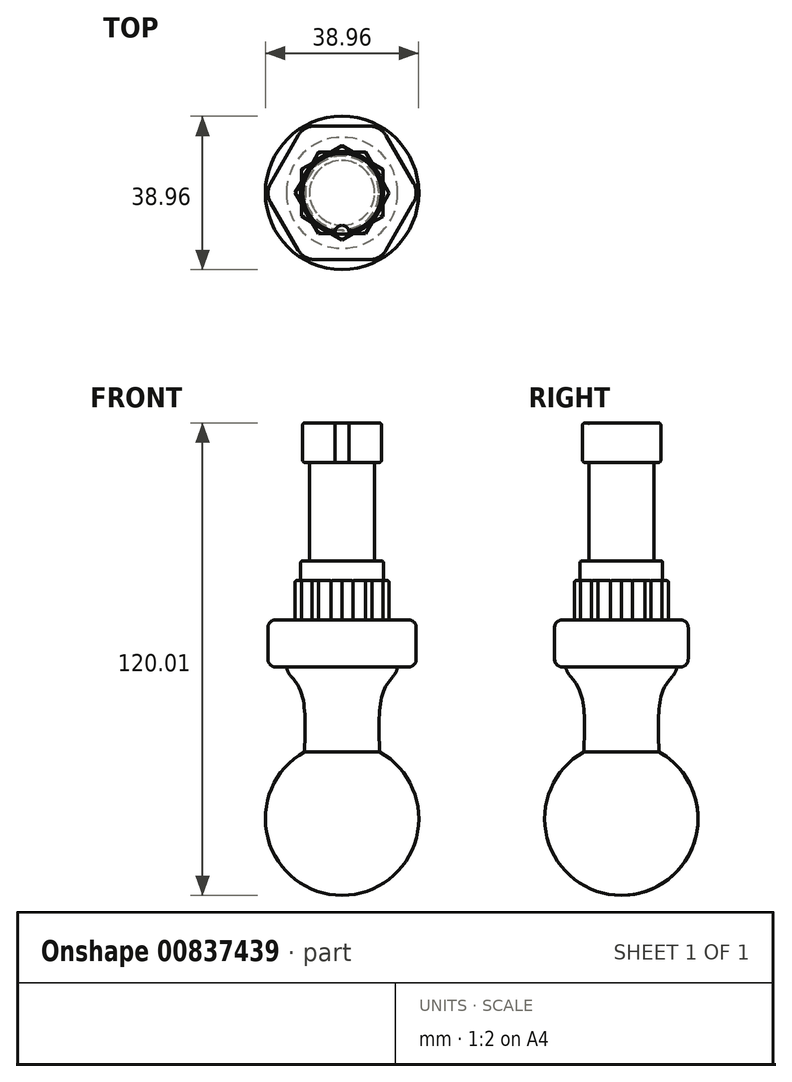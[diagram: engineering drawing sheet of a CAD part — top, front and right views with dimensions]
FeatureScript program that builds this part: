
annotation { "Feature Type Name" : "Feature", "Feature Type Description" : "" }
export const myFeature = defineFeature(function(context is Context, id is Id, definition is map)
    precondition{}
    {
        {
            var Q0;
            Q0=qCreatedBy(makeId("Top.planeOp"),FACE);
            var sketch = newSketch(context, id + "F0", { "sketchPlane" : qUnion([Q0])});
            skCircle(sketch, "E0.cCircle", {"center": v(0, 0) * mm, "radius": 11.95 * mm, "construction": true});
            skLineSegment(sketch, "E0.0", {"start": v(10.36, 5.96) * mm, "end": v(10.36, 2.75) * mm});
            skLineSegment(sketch, "E0.1", {"start": v(10.34, -6) * mm, "end": v(7.56, -7.6) * mm});
            skLineSegment(sketch, "E0.2", {"start": v(-0.02, -11.95) * mm, "end": v(-2.8, -10.34) * mm});
            skLineSegment(sketch, "E0.3", {"start": v(-10.36, -5.96) * mm, "end": v(-10.36, -2.75) * mm});
            skLineSegment(sketch, "E0.4", {"start": v(-10.34, 6) * mm, "end": v(-7.56, 7.6) * mm});
            skLineSegment(sketch, "E0.5", {"start": v(0.02, 11.95) * mm, "end": v(2.8, 10.34) * mm});
            skLineSegment(sketch, "E1", {"start": v(6, 10.34) * mm, "end": v(6.72, 11.59) * mm, "construction": true});
            skLineSegment(sketch, "E2.0", {"start": v(6, 10.34) * mm, "end": v(7.6, 7.56) * mm});
            skLineSegment(sketch, "E2.1", {"start": v(11.95, -0.02) * mm, "end": v(10.34, -2.8) * mm});
            skLineSegment(sketch, "E2.2", {"start": v(5.96, -10.36) * mm, "end": v(2.75, -10.36) * mm});
            skLineSegment(sketch, "E2.3", {"start": v(-6, -10.34) * mm, "end": v(-7.6, -7.56) * mm});
            skLineSegment(sketch, "E2.4", {"start": v(-11.95, 0.02) * mm, "end": v(-10.34, 2.8) * mm});
            skLineSegment(sketch, "E2.5", {"start": v(-5.96, 10.36) * mm, "end": v(-2.75, 10.36) * mm});
            skLineSegment(sketch, "E3.trimOffspring", {"start": v(-7.6, -7.56) * mm, "end": v(-10.36, -5.96) * mm});
            skPoint(sketch, "E4.orphan", {"position": v(-5.2, -8.95) * mm});
            skLineSegment(sketch, "E5.trimOffspring", {"start": v(-10.36, -2.75) * mm, "end": v(-11.95, 0.02) * mm});
            skLineSegment(sketch, "E6.trimOffspring", {"start": v(-2.8, -10.34) * mm, "end": v(-6, -10.34) * mm});
            skLineSegment(sketch, "E7.trimOffspring", {"start": v(2.75, -10.36) * mm, "end": v(-0.02, -11.95) * mm});
            skLineSegment(sketch, "E8.trimOffspring", {"start": v(7.56, -7.6) * mm, "end": v(5.96, -10.36) * mm});
            skLineSegment(sketch, "E9.trimOffspring", {"start": v(-10.34, 2.8) * mm, "end": v(-10.34, 6) * mm});
            skLineSegment(sketch, "E10.trimOffspring", {"start": v(-7.56, 7.6) * mm, "end": v(-5.96, 10.36) * mm});
            skLineSegment(sketch, "E11.trimOffspring", {"start": v(-2.75, 10.36) * mm, "end": v(0.02, 11.95) * mm});
            skLineSegment(sketch, "E12.trimOffspring", {"start": v(2.8, 10.34) * mm, "end": v(6, 10.34) * mm});
            skLineSegment(sketch, "E13.trimOffspring", {"start": v(7.6, 7.56) * mm, "end": v(10.36, 5.96) * mm});
            skPoint(sketch, "E14.orphan", {"position": v(5.2, 8.95) * mm});
            skLineSegment(sketch, "E15.trimOffspring", {"start": v(10.36, 2.75) * mm, "end": v(11.95, -0.02) * mm});
            skLineSegment(sketch, "E16.trimOffspring", {"start": v(10.34, -2.8) * mm, "end": v(10.34, -6) * mm});
            skSolve(sketch);
        }
        {
            var Q0;
            Q0=makeQuery(id+"F0.imprint","IMPRINT",FACE,{"disambiguationData":[TD([[makeQuery(id+"F0.imprint","IMPRINT",EDGE,{"derivedFrom":sQuery(id+"F0.wireOp",EDGE,"E0.0")}),-1.0]])]});
            extrude(context, id + "F1", {"entities" : qUnion([Q0]), "depth" : 10 * mm, "offsetDistance" : 25 * mm});
        }
        {
            var Q0;
            Q0=makeQuery(id+"F1.opExtrude","CAP_FACE",FACE,{"disambiguationData":[OSD([sQuery(id+"F0.wireOp",EDGE,"E0.0"),sQuery(id+"F0.wireOp",EDGE,"E0.1"),sQuery(id+"F0.wireOp",EDGE,"E0.2"),sQuery(id+"F0.wireOp",EDGE,"E0.3"),sQuery(id+"F0.wireOp",EDGE,"E0.4"),sQuery(id+"F0.wireOp",EDGE,"E0.5"),sQuery(id+"F0.wireOp",EDGE,"E2.0"),sQuery(id+"F0.wireOp",EDGE,"E2.1"),sQuery(id+"F0.wireOp",EDGE,"E2.2"),sQuery(id+"F0.wireOp",EDGE,"E2.3"),sQuery(id+"F0.wireOp",EDGE,"E2.4"),sQuery(id+"F0.wireOp",EDGE,"E2.5"),sQuery(id+"F0.wireOp",EDGE,"E3.trimOffspring"),sQuery(id+"F0.wireOp",EDGE,"E5.trimOffspring"),sQuery(id+"F0.wireOp",EDGE,"E6.trimOffspring"),sQuery(id+"F0.wireOp",EDGE,"E7.trimOffspring"),sQuery(id+"F0.wireOp",EDGE,"E8.trimOffspring"),sQuery(id+"F0.wireOp",EDGE,"E9.trimOffspring"),sQuery(id+"F0.wireOp",EDGE,"E10.trimOffspring"),sQuery(id+"F0.wireOp",EDGE,"E11.trimOffspring"),sQuery(id+"F0.wireOp",EDGE,"E12.trimOffspring"),sQuery(id+"F0.wireOp",EDGE,"E13.trimOffspring"),sQuery(id+"F0.wireOp",EDGE,"E15.trimOffspring"),sQuery(id+"F0.wireOp",EDGE,"E16.trimOffspring")])],"isStart":false});
            var sketch = newSketch(context, id + "F2", { "sketchPlane" : qUnion([Q0])});
            skLineSegment(sketch, "E17", {"start": v(-10.36, -2.75) * mm, "end": v(10.36, 2.75) * mm, "construction": true});
            skLineSegment(sketch, "E18", {"start": v(2.75, -10.36) * mm, "end": v(-2.75, 10.36) * mm, "construction": true});
            skCircle(sketch, "E19", {"center": v(0, 0) * mm, "radius": 10.5 * mm});
            skSolve(sketch);
        }
        {
            var Q0;
            Q0=makeQuery(id+"F2.imprint","IMPRINT",FACE,{"disambiguationData":[TD([[makeQuery(id+"F2.imprint","IMPRINT",EDGE,{"derivedFrom":sQuery(id+"F2.wireOp",EDGE,"E19")}),1.0]])]});
            extrude(context, id + "F3", {"entities" : qUnion([Q0]), "operationType" : NewBodyOperationType.ADD, "depth" : 5 * mm, "offsetDistance" : 25 * mm});
        }
        {
            var Q0;
            Q0=makeQuery(id+"F1.opExtrude","CAP_EDGE",EDGE,{"disambiguationData":[OSD([sQuery(id+"F0.wireOp",EDGE,"E2.5")])],"isStart":false});
            var Q1;
            Q1=makeQuery(id+"F1.opExtrude","CAP_EDGE",EDGE,{"disambiguationData":[OSD([sQuery(id+"F0.wireOp",EDGE,"E10.trimOffspring")])],"isStart":false});
            var Q2;
            Q2=makeQuery(id+"F1.opExtrude","CAP_EDGE",EDGE,{"disambiguationData":[OSD([sQuery(id+"F0.wireOp",EDGE,"E0.4")])],"isStart":false});
            var Q3;
            Q3=makeQuery(id+"F1.opExtrude","CAP_EDGE",EDGE,{"disambiguationData":[OSD([sQuery(id+"F0.wireOp",EDGE,"E9.trimOffspring")])],"isStart":false});
            var Q4;
            Q4=makeQuery(id+"F1.opExtrude","CAP_EDGE",EDGE,{"disambiguationData":[OSD([sQuery(id+"F0.wireOp",EDGE,"E2.4")])],"isStart":false});
            var Q5;
            Q5=makeQuery(id+"F1.opExtrude","CAP_EDGE",EDGE,{"disambiguationData":[OSD([sQuery(id+"F0.wireOp",EDGE,"E5.trimOffspring")])],"isStart":false});
            var Q6;
            Q6=makeQuery(id+"F1.opExtrude","CAP_EDGE",EDGE,{"disambiguationData":[OSD([sQuery(id+"F0.wireOp",EDGE,"E0.3")])],"isStart":false});
            var Q7;
            Q7=makeQuery(id+"F1.opExtrude","CAP_EDGE",EDGE,{"disambiguationData":[OSD([sQuery(id+"F0.wireOp",EDGE,"E3.trimOffspring")])],"isStart":false});
            var Q8;
            Q8=makeQuery(id+"F1.opExtrude","CAP_EDGE",EDGE,{"disambiguationData":[OSD([sQuery(id+"F0.wireOp",EDGE,"E2.3")])],"isStart":false});
            var Q9;
            Q9=makeQuery(id+"F1.opExtrude","CAP_EDGE",EDGE,{"disambiguationData":[OSD([sQuery(id+"F0.wireOp",EDGE,"E6.trimOffspring")])],"isStart":false});
            var Q10;
            Q10=makeQuery(id+"F1.opExtrude","CAP_EDGE",EDGE,{"disambiguationData":[OSD([sQuery(id+"F0.wireOp",EDGE,"E0.2")])],"isStart":false});
            var Q11;
            Q11=makeQuery(id+"F1.opExtrude","CAP_EDGE",EDGE,{"disambiguationData":[OSD([sQuery(id+"F0.wireOp",EDGE,"E7.trimOffspring")])],"isStart":false});
            var Q12;
            Q12=makeQuery(id+"F1.opExtrude","CAP_EDGE",EDGE,{"disambiguationData":[OSD([sQuery(id+"F0.wireOp",EDGE,"E2.2")])],"isStart":false});
            var Q13;
            Q13=makeQuery(id+"F1.opExtrude","CAP_EDGE",EDGE,{"disambiguationData":[OSD([sQuery(id+"F0.wireOp",EDGE,"E8.trimOffspring")])],"isStart":false});
            var Q14;
            Q14=makeQuery(id+"F1.opExtrude","CAP_EDGE",EDGE,{"disambiguationData":[OSD([sQuery(id+"F0.wireOp",EDGE,"E0.1")])],"isStart":false});
            var Q15;
            Q15=makeQuery(id+"F1.opExtrude","CAP_EDGE",EDGE,{"disambiguationData":[OSD([sQuery(id+"F0.wireOp",EDGE,"E16.trimOffspring")])],"isStart":false});
            var Q16;
            Q16=makeQuery(id+"F1.opExtrude","CAP_EDGE",EDGE,{"disambiguationData":[OSD([sQuery(id+"F0.wireOp",EDGE,"E2.1")])],"isStart":false});
            var Q17;
            Q17=makeQuery(id+"F1.opExtrude","CAP_EDGE",EDGE,{"disambiguationData":[OSD([sQuery(id+"F0.wireOp",EDGE,"E15.trimOffspring")])],"isStart":false});
            var Q18;
            Q18=makeQuery(id+"F1.opExtrude","CAP_EDGE",EDGE,{"disambiguationData":[OSD([sQuery(id+"F0.wireOp",EDGE,"E0.0")])],"isStart":false});
            var Q19;
            Q19=makeQuery(id+"F1.opExtrude","CAP_EDGE",EDGE,{"disambiguationData":[OSD([sQuery(id+"F0.wireOp",EDGE,"E13.trimOffspring")])],"isStart":false});
            var Q20;
            Q20=makeQuery(id+"F1.opExtrude","CAP_EDGE",EDGE,{"disambiguationData":[OSD([sQuery(id+"F0.wireOp",EDGE,"E2.0")])],"isStart":false});
            var Q21;
            Q21=makeQuery(id+"F1.opExtrude","CAP_EDGE",EDGE,{"disambiguationData":[OSD([sQuery(id+"F0.wireOp",EDGE,"E12.trimOffspring")])],"isStart":false});
            var Q22;
            Q22=makeQuery(id+"F1.opExtrude","CAP_EDGE",EDGE,{"disambiguationData":[OSD([sQuery(id+"F0.wireOp",EDGE,"E0.5")])],"isStart":false});
            var Q23;
            Q23=makeQuery(id+"F1.opExtrude","CAP_EDGE",EDGE,{"disambiguationData":[OSD([sQuery(id+"F0.wireOp",EDGE,"E11.trimOffspring")])],"isStart":false});
            fillet(context, id + "F4", {"entities" : qUnion([Q0, Q1, Q2, Q3, Q4, Q5, Q6, Q7, Q8, Q9, Q10, Q11, Q12, Q13, Q14, Q15, Q16, Q17, Q18, Q19, Q20, Q21, Q22, Q23]), "radius" : .5 * mm, "tangentPropagation" : true, "allowEdgeOverflow" : false});
        }
        {
            var Q0;
            Q0=makeQuery(id+"F3.opExtrude","CAP_FACE",FACE,{"disambiguationData":[OSD([sQuery(id+"F2.wireOp",EDGE,"E19")])],"isStart":false});
            var sketch = newSketch(context, id + "F5", { "sketchPlane" : qUnion([Q0])});
            skCircle(sketch, "E20", {"center": v(0, 0) * mm, "radius": 8.25 * mm});
            skSolve(sketch);
        }
        {
            var Q0;
            Q0=makeQuery(id+"F5.imprint","IMPRINT",FACE,{"disambiguationData":[TD([[makeQuery(id+"F5.imprint","IMPRINT",EDGE,{"derivedFrom":sQuery(id+"F5.wireOp",EDGE,"E20")}),1.0]])]});
            extrude(context, id + "F6", {"entities" : qUnion([Q0]), "operationType" : NewBodyOperationType.ADD, "depth" : 25 * mm, "offsetDistance" : 25 * mm});
        }
        {
            var Q0;
            Q0=makeQuery(id+"F6.opExtrude","CAP_FACE",FACE,{"disambiguationData":[OSD([sQuery(id+"F5.wireOp",EDGE,"E20")])],"isStart":false});
            var sketch = newSketch(context, id + "F7", { "sketchPlane" : qUnion([Q0])});
            skCircle(sketch, "E21", {"center": v(0, 0) * mm, "radius": 10 * mm});
            skSolve(sketch);
        }
        {
            var Q0;
            Q0=makeQuery(id+"F7.imprint","IMPRINT",FACE,{"disambiguationData":[TD([[makeQuery(id+"F7.imprint","IMPRINT",EDGE,{"derivedFrom":sQuery(id+"F7.wireOp",EDGE,"E21")}),1.0]])]});
            var Q1;
            Q1=makeQuery(id+"F7.imprint","IMPRINT",FACE,{"disambiguationData":[TD([[makeQuery(id+"F7.imprint","IMPRINT",EDGE,{"derivedFrom":makeQuery(id+"F6.opExtrude","CAP_EDGE",EDGE,{"disambiguationData":[OSD([sQuery(id+"F5.wireOp",EDGE,"E20")])],"isStart":false})}),1.0]])]});
            extrude(context, id + "F8", {"entities" : qUnion([Q0, Q1]), "operationType" : NewBodyOperationType.ADD, "depth" : 10 * mm, "offsetDistance" : 25 * mm});
        }
        {
            var Q0;
            Q0=makeQuery(id+"F8.opExtrude","CAP_FACE",FACE,{"disambiguationData":[OSD([sQuery(id+"F7.wireOp",EDGE,"E21")])],"isStart":true});
            var sketch = newSketch(context, id + "F9", { "sketchPlane" : qUnion([Q0])});
            skLineSegment(sketch, "E22", {"start": v(0, 10) * mm, "end": v(0, 8.25) * mm, "construction": true});
            skArc(sketch, "E23", {"start": v(0, 8.25) * mm, "mid": v(1.18, 8.7) * mm, "end": v(1.74, 9.85) * mm});
            skArc(sketch, "E24", {"start": v(0, 8.25) * mm, "mid": v(-1.18, 8.7) * mm, "end": v(-1.74, 9.85) * mm});
            skSolve(sketch);
        }
        {
            var Q0;
            {var subQ0=sQuery(id+"F9.wireOp",EDGE,"E23");Q0=makeQuery(id+"F9.imprint","IMPRINT",FACE,{"disambiguationData":[TD([[makeQuery(id+"F9.imprint","IMPRINT",EDGE,{"derivedFrom":subQ0}),1.0]])]});}
            extrude(context, id + "F10", {"entities" : qUnion([Q0]), "operationType" : NewBodyOperationType.REMOVE, "oppositeDirection" : true, "depth" : 25 * mm, "offsetDistance" : 25 * mm});
        }
        {
            var Q0;
            Q0=makeQuery(id+"F8.opExtrude","CAP_EDGE",EDGE,{"disambiguationData":[OSD([sQuery(id+"F7.wireOp",EDGE,"E21")])],"isStart":false});
            var Q1;
            Q1=makeQuery(id+"F10.boolean.opBoolean","INTERSECT",EDGE,{"derivedFrom":[makeQuery(id+"F8.opExtrude","CAP_FACE",FACE,{"disambiguationData":[OSD([sQuery(id+"F7.wireOp",EDGE,"E21")])],"isStart":false}),makeQuery(id+"F10.opExtrude","SWEPT_FACE",FACE,{"disambiguationData":[OSD([sQuery(id+"F9.wireOp",EDGE,"E23"),sQuery(id+"F9.wireOp",EDGE,"E24")])]})]});
            var Q2;
            Q2=makeQuery(id+"F10.boolean.opBoolean","COPY",EDGE,{"derivedFrom":makeQuery(id+"F10.opExtrude","SWEPT_EDGE",EDGE,{"disambiguationData":[OSD([sQuery(id+"F7.wireOp",EDGE,"E21"),sQuery(id+"F9.wireOp",EDGE,"E24")])]})});
            var Q3;
            Q3=makeQuery(id+"F10.boolean.opBoolean","COPY",EDGE,{"derivedFrom":makeQuery(id+"F10.opExtrude","SWEPT_EDGE",EDGE,{"disambiguationData":[OSD([sQuery(id+"F7.wireOp",EDGE,"E21"),sQuery(id+"F9.wireOp",EDGE,"E23")])]})});
            var Q4;
            Q4=makeQuery(id+"F8.opExtrude","CAP_EDGE",EDGE,{"disambiguationData":[OSD([sQuery(id+"F7.wireOp",EDGE,"E21")])],"isStart":true});
            var Q5;
            Q5=makeQuery(id+"F10.boolean.opBoolean","COPY",EDGE,{"disambiguationData":[OD(1.0)],"derivedFrom":makeQuery(id+"F10.opExtrude","CAP_EDGE",EDGE,{"disambiguationData":[OSD([sQuery(id+"F9.wireOp",EDGE,"E23"),sQuery(id+"F9.wireOp",EDGE,"E24")])],"isStart":true})});
            var Q6;
            Q6=makeQuery(id+"F10.boolean.opBoolean","COPY",EDGE,{"disambiguationData":[OD(0.0)],"derivedFrom":makeQuery(id+"F10.opExtrude","CAP_EDGE",EDGE,{"disambiguationData":[OSD([sQuery(id+"F9.wireOp",EDGE,"E23"),sQuery(id+"F9.wireOp",EDGE,"E24")])],"isStart":true})});
            fillet(context, id + "F11", {"entities" : qUnion([Q0, Q1, Q2, Q3, Q4, Q5, Q6]), "radius" : .5 * mm, "tangentPropagation" : true, "allowEdgeOverflow" : false});
        }
        {
            var Q0;
            Q0=makeQuery(id+"F6.opExtrude","CAP_EDGE",EDGE,{"disambiguationData":[OSD([sQuery(id+"F5.wireOp",EDGE,"E20")])],"isStart":true});
            var Q1;
            Q1=makeQuery(id+"F3.opExtrude","CAP_EDGE",EDGE,{"disambiguationData":[OSD([sQuery(id+"F2.wireOp",EDGE,"E19")])],"isStart":false});
            fillet(context, id + "F12", {"entities" : qUnion([Q0, Q1]), "radius" : .5 * mm, "tangentPropagation" : true, "allowEdgeOverflow" : false});
        }
        {
            var Q0;
            Q0=makeQuery(id+"F1.opExtrude","CAP_FACE",FACE,{"disambiguationData":[OSD([sQuery(id+"F0.wireOp",EDGE,"E0.0"),sQuery(id+"F0.wireOp",EDGE,"E0.1"),sQuery(id+"F0.wireOp",EDGE,"E0.2"),sQuery(id+"F0.wireOp",EDGE,"E0.3"),sQuery(id+"F0.wireOp",EDGE,"E0.4"),sQuery(id+"F0.wireOp",EDGE,"E0.5"),sQuery(id+"F0.wireOp",EDGE,"E2.0"),sQuery(id+"F0.wireOp",EDGE,"E2.1"),sQuery(id+"F0.wireOp",EDGE,"E2.2"),sQuery(id+"F0.wireOp",EDGE,"E2.3"),sQuery(id+"F0.wireOp",EDGE,"E2.4"),sQuery(id+"F0.wireOp",EDGE,"E2.5"),sQuery(id+"F0.wireOp",EDGE,"E3.trimOffspring"),sQuery(id+"F0.wireOp",EDGE,"E5.trimOffspring"),sQuery(id+"F0.wireOp",EDGE,"E6.trimOffspring"),sQuery(id+"F0.wireOp",EDGE,"E7.trimOffspring"),sQuery(id+"F0.wireOp",EDGE,"E8.trimOffspring"),sQuery(id+"F0.wireOp",EDGE,"E9.trimOffspring"),sQuery(id+"F0.wireOp",EDGE,"E10.trimOffspring"),sQuery(id+"F0.wireOp",EDGE,"E11.trimOffspring"),sQuery(id+"F0.wireOp",EDGE,"E12.trimOffspring"),sQuery(id+"F0.wireOp",EDGE,"E13.trimOffspring"),sQuery(id+"F0.wireOp",EDGE,"E15.trimOffspring"),sQuery(id+"F0.wireOp",EDGE,"E16.trimOffspring")])],"isStart":true});
            var sketch = newSketch(context, id + "F13", { "sketchPlane" : qUnion([Q0])});
            skCircle(sketch, "E25.cCircle", {"center": v(0, 0) * mm, "radius": 16.96 * mm, "construction": true});
            skLineSegment(sketch, "E25.0", {"start": v(-11.22, -14.53) * mm, "end": v(-18.17, -2.4) * mm});
            skLineSegment(sketch, "E25.1", {"start": v(-18.16, 2.5) * mm, "end": v(-11.17, 14.54) * mm});
            skLineSegment(sketch, "E25.2", {"start": v(-6.92, 16.98) * mm, "end": v(7.06, 16.94) * mm});
            skLineSegment(sketch, "E25.3", {"start": v(11.22, 14.53) * mm, "end": v(18.2, 2.35) * mm});
            skLineSegment(sketch, "E25.4", {"start": v(18.2, -2.45) * mm, "end": v(11.17, -14.54) * mm});
            skLineSegment(sketch, "E25.5", {"start": v(6.92, -16.98) * mm, "end": v(-7.06, -16.94) * mm});
            skPoint(sketch, "E25.0.midPoint", {"position": v(-14.7, -8.44) * mm});
            skPoint(sketch, "E26.visualSharp", {"position": v(9.75, -16.99) * mm});
            skArc(sketch, "E26.filletArc", {"start": v(6.92, -16.98) * mm, "mid": v(9.37, -16.33) * mm, "end": v(11.17, -14.54) * mm});
            skPoint(sketch, "E27.visualSharp", {"position": v(-9.84, -16.93) * mm});
            skArc(sketch, "E27.filletArc", {"start": v(-11.22, -14.53) * mm, "mid": v(-9.46, -16.3) * mm, "end": v(-7.06, -16.94) * mm});
            skPoint(sketch, "E28.visualSharp", {"position": v(-19.58, 0.05) * mm});
            skArc(sketch, "E28.filletArc", {"start": v(-18.16, 2.5) * mm, "mid": v(-18.82, 0.05) * mm, "end": v(-18.17, -2.4) * mm});
            skPoint(sketch, "E29.visualSharp", {"position": v(-9.75, 16.99) * mm});
            skArc(sketch, "E29.filletArc", {"start": v(-6.92, 16.98) * mm, "mid": v(-9.37, 16.33) * mm, "end": v(-11.17, 14.54) * mm});
            skPoint(sketch, "E30.visualSharp", {"position": v(9.84, 16.93) * mm});
            skArc(sketch, "E30.filletArc", {"start": v(11.22, 14.53) * mm, "mid": v(9.46, 16.3) * mm, "end": v(7.06, 16.94) * mm});
            skPoint(sketch, "E31.visualSharp", {"position": v(19.58, -0.05) * mm});
            skArc(sketch, "E31.filletArc", {"start": v(18.2, -2.45) * mm, "mid": v(18.84, -0.05) * mm, "end": v(18.2, 2.35) * mm});
            skSolve(sketch);
        }
        {
            var Q0;
            Q0=makeQuery(id+"F13.imprint","IMPRINT",FACE,{"disambiguationData":[TD([[makeQuery(id+"F13.imprint","IMPRINT",EDGE,{"derivedFrom":sQuery(id+"F13.wireOp",EDGE,"XwkZxwQT-tXsu-qyU6-IrZG-78iqKTn2pKXx")}),1.0]])]});
            var Q1;
            Q1=makeQuery(id+"F13.imprint","IMPRINT",FACE,{"disambiguationData":[TD([[makeQuery(id+"F13.imprint","IMPRINT",EDGE,{"derivedFrom":makeQuery(id+"F1.opExtrude","CAP_EDGE",EDGE,{"disambiguationData":[OSD([sQuery(id+"F0.wireOp",EDGE,"E0.0")])],"isStart":true})}),1.0]])]});
            var Q2;
            Q2=makeQuery(id+"F13.imprint","IMPRINT",FACE,{"disambiguationData":[TD([[makeQuery(id+"F13.imprint","IMPRINT",EDGE,{"derivedFrom":sQuery(id+"F13.wireOp",EDGE,"E25.0")}),-1.0]])]});
            extrude(context, id + "F14", {"entities" : qUnion([Q0, Q1, Q2]), "operationType" : NewBodyOperationType.ADD, "depth" : 12 * mm, "offsetDistance" : 25 * mm});
        }
        {
            var Q0;
            Q0=makeQuery(id+"F14.opExtrude","CAP_EDGE",EDGE,{"disambiguationData":[OSD([sQuery(id+"F13.wireOp",EDGE,"XwkZxwQT-tXsu-qyU6-IrZG-78iqKTn2pKXx")])],"isStart":false});
            var Q1;
            Q1=makeQuery(id+"F14.opExtrude","CAP_EDGE",EDGE,{"disambiguationData":[OSD([sQuery(id+"F13.wireOp",EDGE,"XwkZxwQT-tXsu-qyU6-IrZG-78iqKTn2pKXx")])],"isStart":true});
            var Q2;
            Q2=makeQuery(id+"F14.opExtrude","CAP_EDGE",EDGE,{"disambiguationData":[OSD([sQuery(id+"F13.wireOp",EDGE,"E25.3")])],"isStart":false});
            var Q3;
            Q3=makeQuery(id+"F14.opExtrude","CAP_EDGE",EDGE,{"disambiguationData":[OSD([sQuery(id+"F13.wireOp",EDGE,"E25.3")])],"isStart":true});
            fillet(context, id + "F15", {"entities" : qUnion([Q0, Q1, Q2, Q3]), "radius" : 2 * mm, "tangentPropagation" : true, "allowEdgeOverflow" : false});
        }
        {
            var Q0;
            Q0=qCreatedBy(makeId("Right.planeOp"),FACE);
            var sketch = newSketch(context, id + "F16", { "sketchPlane" : qUnion([Q0])});
            skLineSegment(sketch, "E32", {"start": v(0, 0) * mm, "end": v(0, -58.93) * mm});
            skPoint(sketch, "E33.orphan", {"position": v(0, -54.24) * mm});
            skPoint(sketch, "E34.end.orphan", {"position": v(0, -52.5) * mm});
            skArc(sketch, "E35", {"start": v(13.72, -64.36) * mm, "mid": v(19.3, -47.92) * mm, "end": v(9.56, -33.55) * mm});
            skLineSegment(sketch, "E36", {"start": v(0, -12.6) * mm, "end": v(0, -64.36) * mm});
            skLineSegment(sketch, "E37", {"start": v(0, -11.95) * mm, "end": v(14.13, -11.95) * mm});
            skPoint(sketch, "E38.1.internal.orphan", {"position": v(14.13, -15.04) * mm});
            skPoint(sketch, "E39.orphan", {"position": v(14.13, -12.6) * mm});
            skLineSegment(sketch, "E40", {"start": v(14.13, -11.95) * mm, "end": v(14.13, -13.15) * mm});
            skFitSpline(sketch, "E41", {"points": [v(14.13, -13.15) * mm, v(10.35, -18.6) * mm, v(9.56, -33.55) * mm], "startDerivative": vector(-11.08, -11.39) * mm, "endDerivative": vector(1.12, -28.29) * mm});
            skArc(sketch, "E42", {"start": v(0, -70.01) * mm, "mid": v(18.85, -55.47) * mm, "end": v(9.56, -33.55) * mm});
            skLineSegment(sketch, "E43", {"start": v(0, -36.24) * mm, "end": v(0, -76.23) * mm});
            skSolve(sketch);
        }
        {
            var Q0;
            {var subQ1=sQuery(id+"F16.wireOp",EDGE,"NLwjia8V-UTQ4-TUgC-SJFi-TH08i8K1N5aU");Q0=makeQuery(id+"F16.imprint","IMPRINT",FACE,{"disambiguationData":[TD([[makeQuery(id+"F16.imprint","IMPRINT",EDGE,{"derivedFrom":subQ1}),-1.0]])]});}
            var Q1;
            Q1=makeQuery(id+"F16.imprint","IMPRINT",FACE,{"disambiguationData":[TD([[makeQuery(id+"F16.imprint","IMPRINT",EDGE,{"derivedFrom":sQuery(id+"F16.wireOp",EDGE,"E35")}),1.0]])]});
            var Q2;
            {var subQ1=sQuery(id+"F16.wireOp",EDGE,"E36");Q2=makeQuery(id+"F16.imprint","IMPRINT",FACE,{"disambiguationData":[TD([[makeQuery(id+"F16.imprint","IMPRINT",EDGE,{"derivedFrom":subQ1}),1.0]])]});}
            var Q3;
            Q3=sQuery(id+"F16.wireOp",EDGE,"E32");
            revolve(context, id + "F17", {"operationType" : NewBodyOperationType.ADD, "surfaceOperationType" : NewSurfaceOperationType.NEW, "entities" : qUnion([Q0, Q1, Q2]), "axis" : qUnion([Q3]), "revolveType" : RevolveType.FULL});
        }
        {
            var Q0;
            Q0=makeQuery(id+"F17.opRevolve","SWEPT_EDGE",EDGE,{"disambiguationData":[OSD([sQuery(id+"F16.wireOp",EDGE,"E40"),sQuery(id+"F16.wireOp",EDGE,"E41")])]});
            fillet(context, id + "F18", {"entities" : qUnion([Q0]), "radius" : 5 * mm, "tangentPropagation" : true, "allowEdgeOverflow" : false});
        }
    });
